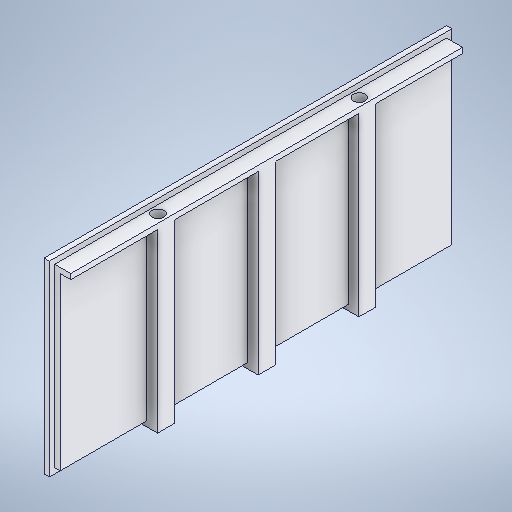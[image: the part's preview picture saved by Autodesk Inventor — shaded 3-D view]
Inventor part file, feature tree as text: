
AUTODESK INVENTOR PART (.ipt)
format: ipt  version: 2025 (Build 290162000, 162)  size: 350,208 bytes
history: native  units: in
note: dims shown in document units (in); Inventor stores cm internally (conversion verified against a paired STEP export)
features: projected_geometry x8, extrude x7, sketch x7
ambient origin geometry x8: Origin, YZ Plane, XZ Plane, XY Plane, X Axis, Y Axis, Z Axis, Center Point
bodies: Solid1 (feature_tree)
feature tree (22):
  extrude  "Extrusion1"  Depth=5.9213in
  extrude  "Extrusion2"  Depth=0.0787in
  extrude  "Extrusion3"  Depth=0.0787in
  extrude  "Extrusion4"  Depth=0.25in
  extrude  "Extrusion5"  Depth=0.25in
  extrude  "Extrusion6"  Depth=0.0787in TaperAngle=0.0deg
  extrude  "Extrusion7"  Depth=0.0787in TaperAngle=0.0deg
  sketch  "Sketch1"  dims[d0=2.75in d1=5.9213in]
  sketch  "Sketch2"  dims[d2=0.0787in d3=0.0in d4=0.0787in]
  projected_geometry  "Projected Loop1"
  sketch  "Sketch3"  dims[d5=0.0787in d6=0.0787in]
  projected_geometry  "Projected Loop2"
  sketch  "Sketch4"  dims[d7=0.0787in d8=0.0in d9=0.25in]
  projected_geometry  "Projected Loop3"
  sketch  "Sketch5"  dims[d10=0.25in d11=0.25in]
  projected_geometry  "Projected Loop4"
  sketch  "Sketch7"  dims[d12=0.1575in d13=0.0in d14=0.0787in d15=0.0in]
  projected_geometry  "Projected Loop5"
  projected_geometry  "Projected Loop6"
  projected_geometry  "Projected Loop7"
  sketch  "Sketch8"  dims[d16=0.0787in d17=0.0in d18=0.0787in d19=0.0in d20=0.1772in d21=0.1772in d22=0.1969in d23=0.0in]
  projected_geometry  "Projected Loop8"
